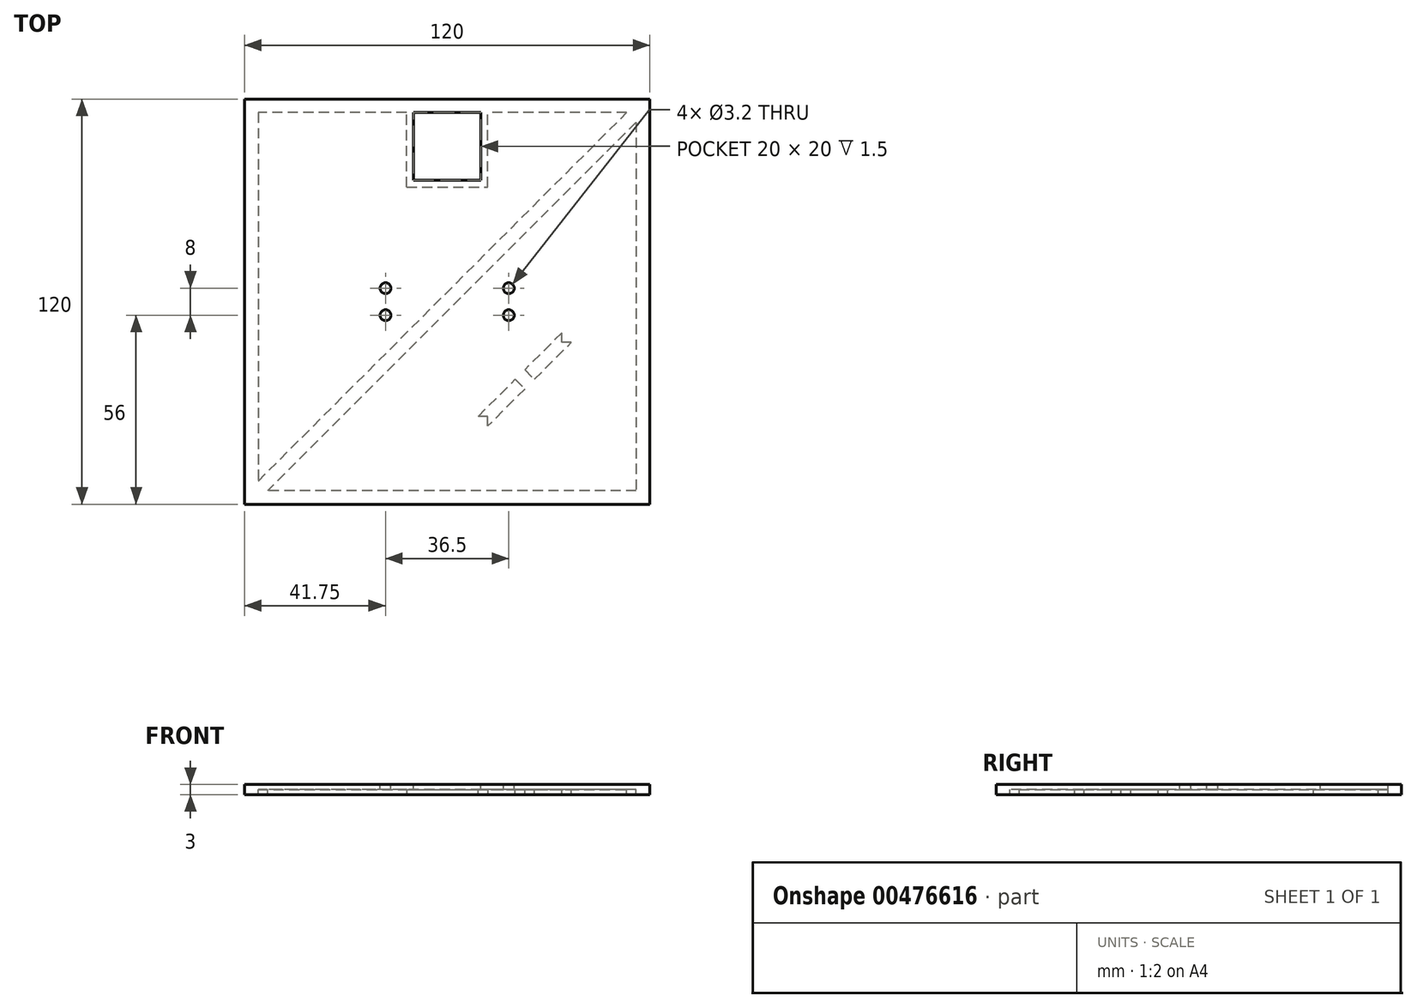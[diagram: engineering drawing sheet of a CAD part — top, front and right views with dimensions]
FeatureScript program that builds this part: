
annotation { "Feature Type Name" : "Feature", "Feature Type Description" : "" }
export const myFeature = defineFeature(function(context is Context, id is Id, definition is map)
    precondition{}
    {
        {
            var Q0;
            Q0=qCreatedBy(makeId("Top.planeOp"),FACE);
            var sketch = newSketch(context, id + "F0", { "sketchPlane" : qUnion([Q0])});
            skLineSegment(sketch, "E0.bottom", {"start": v(60, 60) * mm, "end": v(-60, 60) * mm});
            skLineSegment(sketch, "E0.top", {"start": v(60, -60) * mm, "end": v(-60, -60) * mm});
            skLineSegment(sketch, "E0.left", {"start": v(60, 60) * mm, "end": v(60, -60) * mm});
            skLineSegment(sketch, "E0.right", {"start": v(-60, 60) * mm, "end": v(-60, -60) * mm});
            skPoint(sketch, "E0.middle", {"position": v(0, 0) * mm});
            skSolve(sketch);
        }
        {
            var Q0;
            Q0 = qSketchRegion(id + "F0", true);
            extrude(context, id + "F1", {"entities" : qUnion([Q0]), "depth" : 1.5 * mm});
        }
        {
            var Q0;
            Q0=makeQuery(id+"F1.opExtrude","CAP_FACE",FACE,{"disambiguationData":[OSD([sQuery(id+"F0.wireOp",EDGE,"E0.bottom"),sQuery(id+"F0.wireOp",EDGE,"E0.top"),sQuery(id+"F0.wireOp",EDGE,"E0.left"),sQuery(id+"F0.wireOp",EDGE,"E0.right")])],"isStart":false});
            var sketch = newSketch(context, id + "F2", { "sketchPlane" : qUnion([Q0])});
            skLineSegment(sketch, "E1.bottom", {"start": v(10, 56) * mm, "end": v(-10, 56) * mm});
            skLineSegment(sketch, "E1.top", {"start": v(10, 36) * mm, "end": v(-10, 36) * mm});
            skLineSegment(sketch, "E1.left", {"start": v(10, 56) * mm, "end": v(10, 36) * mm});
            skLineSegment(sketch, "E1.right", {"start": v(-10, 56) * mm, "end": v(-10, 36) * mm});
            skPoint(sketch, "E1.middle", {"position": v(0, 46) * mm});
            skSolve(sketch);
        }
        {
            var Q0;
            Q0=qCreatedBy(makeId("Front.planeOp"),FACE);
            var sketch = newSketch(context, id + "F3", { "sketchPlane" : qUnion([Q0])});
            skLineSegment(sketch, "E2", {"start": v(0, 0) * mm, "end": v(0, 21.35) * mm});
            skSolve(sketch);
        }
        {
            var Q0;
            Q0=makeQuery(id+"F1.opExtrude","CAP_FACE",FACE,{"disambiguationData":[OSD([sQuery(id+"F0.wireOp",EDGE,"E0.bottom"),sQuery(id+"F0.wireOp",EDGE,"E0.top"),sQuery(id+"F0.wireOp",EDGE,"E0.left"),sQuery(id+"F0.wireOp",EDGE,"E0.right")])],"isStart":true});
            var sketch = newSketch(context, id + "F4", { "sketchPlane" : qUnion([Q0])});
            skLineSegment(sketch, "E3.bottom", {"start": v(-12, -34) * mm, "end": v(12, -34) * mm});
            skLineSegment(sketch, "E3.top", {"start": v(-12, -58) * mm, "end": v(12, -58) * mm});
            skLineSegment(sketch, "E3.left", {"start": v(-12, -34) * mm, "end": v(-12, -58) * mm});
            skLineSegment(sketch, "E3.right", {"start": v(12, -34) * mm, "end": v(12, -58) * mm});
            skPoint(sketch, "E3.middle", {"position": v(0, -46) * mm});
            skSolve(sketch);
        }
        {
            var Q0;
            Q0=makeQuery(id+"F4.imprint","IMPRINT",FACE,{"disambiguationData":[TD([[makeQuery(id+"F4.imprint","IMPRINT",EDGE,{"derivedFrom":sQuery(id+"F4.wireOp",EDGE,"E3.bottom")}),1.0]])]});
            var sketch = newSketch(context, id + "F5", { "sketchPlane" : qUnion([Q0])});
            skLineSegment(sketch, "E4.bottom", {"start": v(60, -60) * mm, "end": v(-60, -60) * mm});
            skLineSegment(sketch, "E4.top", {"start": v(60, 60) * mm, "end": v(-60, 60) * mm});
            skLineSegment(sketch, "E4.left", {"start": v(60, -60) * mm, "end": v(60, 60) * mm});
            skLineSegment(sketch, "E4.right", {"start": v(-60, -60) * mm, "end": v(-60, 60) * mm});
            skPoint(sketch, "E4.middle", {"position": v(0, 0) * mm});
            skLineSegment(sketch, "E5.bottom", {"start": v(56, -56) * mm, "end": v(-56, -56) * mm});
            skLineSegment(sketch, "E5.top", {"start": v(56, 56) * mm, "end": v(-56, 56) * mm});
            skLineSegment(sketch, "E5.left", {"start": v(56, -56) * mm, "end": v(56, 56) * mm});
            skLineSegment(sketch, "E5.right", {"start": v(-56, -56) * mm, "end": v(-56, 56) * mm});
            skSolve(sketch);
        }
        {
            var Q0;
            Q0 = qSketchRegion(id + "F5", true);
            extrude(context, id + "F6", {"entities" : qUnion([Q0]), "operationType" : NewBodyOperationType.ADD, "depth" : 1.5 * mm});
        }
        {
            var Q0;
            Q0 = qSketchRegion(id + "F4", true);
            extrude(context, id + "F7", {"entities" : qUnion([Q0]), "operationType" : NewBodyOperationType.ADD, "depth" : 1.5 * mm});
        }
        {
            var Q0;
            Q0 = qSketchRegion(id + "F2", true);
            extrude(context, id + "F8", {"entities" : qUnion([Q0]), "operationType" : NewBodyOperationType.REMOVE, "oppositeDirection" : true, "depth" : 1.5 * mm});
        }
        {
            var Q0;
            Q0=makeQuery(id+"F1.opExtrude","CAP_FACE",FACE,{"disambiguationData":[OSD([sQuery(id+"F0.wireOp",EDGE,"E0.bottom"),sQuery(id+"F0.wireOp",EDGE,"E0.top"),sQuery(id+"F0.wireOp",EDGE,"E0.left"),sQuery(id+"F0.wireOp",EDGE,"E0.right")])],"isStart":true});
            var sketch = newSketch(context, id + "F9", { "sketchPlane" : qUnion([Q0])});
            skLineSegment(sketch, "E6", {"start": v(-56, 53.17) * mm, "end": v(53.17, -56) * mm});
            skLineSegment(sketch, "E7", {"start": v(53.17, -56) * mm, "end": v(56, -56) * mm});
            skLineSegment(sketch, "E8", {"start": v(56, -56) * mm, "end": v(56, -53.17) * mm});
            skLineSegment(sketch, "E9", {"start": v(56, -53.17) * mm, "end": v(-53.17, 56) * mm});
            skLineSegment(sketch, "E10", {"start": v(-53.17, 56) * mm, "end": v(-56, 56) * mm});
            skLineSegment(sketch, "E11", {"start": v(-56, 56) * mm, "end": v(-56, 53.17) * mm});
            skSolve(sketch);
        }
        {
            var Q0;
            Q0 = qSketchRegion(id + "F9", true);
            extrude(context, id + "F10", {"entities" : qUnion([Q0]), "operationType" : NewBodyOperationType.ADD, "depth" : 1.5 * mm});
        }
        {
            var Q0;
            {var subQ6=makeQuery(id+"F6.opExtrude","SWEPT_FACE",FACE,{"disambiguationData":[OSD([sQuery(id+"F5.wireOp",EDGE,"E5.left")])]});Q0=makeQuery(id+"FsSp5hHmkWeRzvy_1.1.F10.boolean.opBoolean","SPLIT",FACE,{"disambiguationData":[TD([subQ6])],"derivedFrom":makeQuery(id+"F10.boolean.opBoolean","SPLIT",FACE,{"disambiguationData":[TD([makeQuery(id+"F6.opExtrude","SWEPT_FACE",FACE,{"disambiguationData":[OSD([sQuery(id+"F5.wireOp",EDGE,"E5.top")])]})])],"derivedFrom":makeQuery(id+"F1.opExtrude","CAP_FACE",FACE,{"disambiguationData":[OSD([sQuery(id+"F0.wireOp",EDGE,"E0.bottom"),sQuery(id+"F0.wireOp",EDGE,"E0.top"),sQuery(id+"F0.wireOp",EDGE,"E0.left"),sQuery(id+"F0.wireOp",EDGE,"E0.right")])],"isStart":true})})});}
            var sketch = newSketch(context, id + "F11", { "sketchPlane" : qUnion([Q0])});
            skLineSegment(sketch, "E12", {"start": v(34, 12) * mm, "end": v(34, 9.17) * mm});
            skLineSegment(sketch, "E13", {"start": v(34, 9.17) * mm, "end": v(23, 20.17) * mm});
            skLineSegment(sketch, "E14", {"start": v(23, 20.17) * mm, "end": v(25.83, 23) * mm});
            skLineSegment(sketch, "E15", {"start": v(25.83, 23) * mm, "end": v(36.83, 12) * mm});
            skLineSegment(sketch, "E16", {"start": v(36.83, 12) * mm, "end": v(34, 12) * mm});
            skSolve(sketch);
        }
        {
            var Q0;
            Q0 = qSketchRegion(id + "F11", true);
            extrude(context, id + "F12", {"entities" : qUnion([Q0]), "operationType" : NewBodyOperationType.ADD, "depth" : 1.5 * mm});
        }
        {
            var Q0;
            {var subQ3=sQuery(id+"F4.wireOp",EDGE,"E3.bottom");var subQ4=makeQuery(id+"FQJJXGxK85WxdXc_1.2.F7.opExtrude","SWEPT_FACE",FACE,{"disambiguationData":[OSD([subQ3])]});var subQ5=makeQuery(id+"F6.opExtrude","SWEPT_FACE",FACE,{"disambiguationData":[OSD([sQuery(id+"F5.wireOp",EDGE,"E5.top")])]});Q0=makeQuery(id+"FHGUHTgdeMzaSI0_1.3.F12.boolean.opBoolean","SPLIT",FACE,{"disambiguationData":[TD([subQ4])],"derivedFrom":makeQuery(id+"FsSp5hHmkWeRzvy_1.1.F10.boolean.opBoolean","SPLIT",FACE,{"disambiguationData":[TD([subQ5])],"derivedFrom":makeQuery(id+"F10.boolean.opBoolean","SPLIT",FACE,{"disambiguationData":[TD([subQ5])],"derivedFrom":makeQuery(id+"F1.opExtrude","CAP_FACE",FACE,{"disambiguationData":[OSD([sQuery(id+"F0.wireOp",EDGE,"E0.bottom"),sQuery(id+"F0.wireOp",EDGE,"E0.top"),sQuery(id+"F0.wireOp",EDGE,"E0.left"),sQuery(id+"F0.wireOp",EDGE,"E0.right")])],"isStart":true})})})});}
            var sketch = newSketch(context, id + "F13", { "sketchPlane" : qUnion([Q0])});
            skLineSegment(sketch, "E17", {"start": v(12, 34) * mm, "end": v(9.17, 34) * mm});
            skLineSegment(sketch, "E18", {"start": v(9.17, 34) * mm, "end": v(20.17, 23) * mm});
            skLineSegment(sketch, "E19", {"start": v(20.17, 23) * mm, "end": v(23, 25.83) * mm});
            skLineSegment(sketch, "E20", {"start": v(23, 25.83) * mm, "end": v(12, 36.83) * mm});
            skLineSegment(sketch, "E21", {"start": v(12, 36.83) * mm, "end": v(12, 34) * mm});
            skSolve(sketch);
        }
        {
            var Q0;
            Q0 = qSketchRegion(id + "F13", true);
            extrude(context, id + "F14", {"entities" : qUnion([Q0]), "operationType" : NewBodyOperationType.ADD, "depth" : 1.5 * mm});
        }
        {
            var Q0;
            Q0=makeQuery(id+"F1.opExtrude","CAP_FACE",FACE,{"disambiguationData":[OSD([sQuery(id+"F0.wireOp",EDGE,"E0.bottom"),sQuery(id+"F0.wireOp",EDGE,"E0.top"),sQuery(id+"F0.wireOp",EDGE,"E0.left"),sQuery(id+"F0.wireOp",EDGE,"E0.right")])],"isStart":false});
            var sketch = newSketch(context, id + "F15", { "sketchPlane" : qUnion([Q0])});
            skLineSegment(sketch, "E22", {"start": v(10.25, 15.08) * mm, "end": v(10.25, -10.42) * mm});
            skSolve(sketch);
        }
        {
            var Q0;
            Q0=makeQuery(id+"F15.imprint","IMPRINT",FACE,{"disambiguationData":[TD([[makeQuery(id+"F15.imprint","IMPRINT",EDGE,{"derivedFrom":makeQuery(id+"F1.opExtrude","CAP_EDGE",EDGE,{"disambiguationData":[OSD([sQuery(id+"F0.wireOp",EDGE,"E0.bottom")])],"isStart":false})}),1.0]])]});
            var sketch = newSketch(context, id + "F16", { "sketchPlane" : qUnion([Q0])});
            skCircle(sketch, "E23", {"center": v(18.25, 4) * mm, "radius": 1.6 * mm});
            skCircle(sketch, "E24", {"center": v(18.25, -4) * mm, "radius": 1.6 * mm});
            skCircle(sketch, "E25.MirrorC", {"center": v(-18.25, -4) * mm, "radius": 1.6 * mm});
            skCircle(sketch, "E26.MirrorC", {"center": v(-18.25, 4) * mm, "radius": 1.6 * mm});
            skSolve(sketch);
        }
        {
            var Q0;
            Q0 = qSketchRegion(id + "F16", true);
            extrude(context, id + "F17", {"entities" : qUnion([Q0]), "operationType" : NewBodyOperationType.REMOVE, "oppositeDirection" : true, "depth" : 1.5 * mm});
        }
    });
